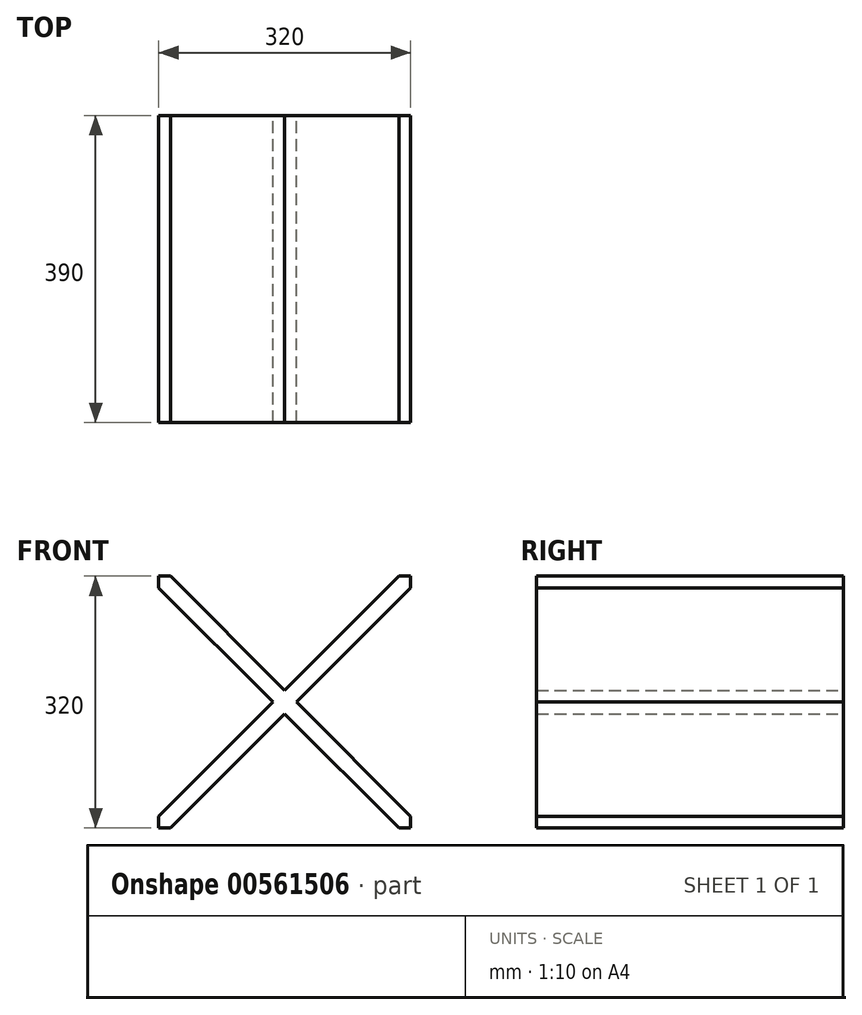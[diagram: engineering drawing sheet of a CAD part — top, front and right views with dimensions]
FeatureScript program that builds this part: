
annotation { "Feature Type Name" : "Feature", "Feature Type Description" : "" }
export const myFeature = defineFeature(function(context is Context, id is Id, definition is map)
    precondition{}
    {
        {
            var Q0;
            Q0=qCreatedBy(makeId("Front.planeOp"),FACE);
            var sketch = newSketch(context, id + "F0", { "sketchPlane" : qUnion([Q0])});
            skLineSegment(sketch, "E0.bottom", {"start": v(0, 0) * mm, "end": v(320, 0) * mm, "construction": true});
            skLineSegment(sketch, "E0.left", {"start": v(0, 0) * mm, "end": v(0, 320) * mm, "construction": true});
            skLineSegment(sketch, "E0.right", {"start": v(320, 0) * mm, "end": v(320, 320) * mm, "construction": true});
            skLineSegment(sketch, "E1", {"start": v(0, 320) * mm, "end": v(320, 0) * mm, "construction": true});
            skLineSegment(sketch, "E2", {"start": v(0, 0) * mm, "end": v(320, 320) * mm, "construction": true});
            skLineSegment(sketch, "E3", {"start": v(320, 320) * mm, "end": v(305, 320) * mm});
            skLineSegment(sketch, "E4", {"start": v(0, 0) * mm, "end": v(0, 15) * mm});
            skLineSegment(sketch, "E5", {"start": v(0, 15) * mm, "end": v(145, 160) * mm});
            skLineSegment(sketch, "E6.trimOffspring", {"start": v(305, 320) * mm, "end": v(320, 320) * mm, "construction": true});
            skLineSegment(sketch, "E7", {"start": v(0, 320) * mm, "end": v(320, 320) * mm, "construction": true});
            skLineSegment(sketch, "E8", {"start": v(0, 0) * mm, "end": v(15, 0) * mm});
            skLineSegment(sketch, "E9", {"start": v(15, 0) * mm, "end": v(160, 145) * mm});
            skLineSegment(sketch, "E10", {"start": v(320, 305) * mm, "end": v(320, 320) * mm});
            skLineSegment(sketch, "E11", {"start": v(0, 320) * mm, "end": v(15, 320) * mm});
            skLineSegment(sketch, "E12", {"start": v(15, 320) * mm, "end": v(320, 15) * mm});
            skLineSegment(sketch, "E13", {"start": v(320, 15) * mm, "end": v(320, 0) * mm});
            skLineSegment(sketch, "E14", {"start": v(320, 0) * mm, "end": v(305, 0) * mm});
            skLineSegment(sketch, "E15", {"start": v(305, 0) * mm, "end": v(160, 145) * mm});
            skLineSegment(sketch, "E16", {"start": v(0, 305) * mm, "end": v(0, 320) * mm});
            skLineSegment(sketch, "E17.trimOffspring", {"start": v(145, 160) * mm, "end": v(0, 305) * mm});
            skLineSegment(sketch, "E18.trimOffspring", {"start": v(175, 160) * mm, "end": v(320, 305) * mm});
            skLineSegment(sketch, "E19.trimOffspring", {"start": v(160, 175) * mm, "end": v(305, 320) * mm});
            skSolve(sketch);
        }
        {
            var Q0;
            Q0 = qSketchRegion(id + "F0", true);
            extrude(context, id + "F1", {"entities" : qUnion([Q0]), "depth" : 390 * mm, "offsetDistance" : 25 * mm, "symmetric" : true});
        }
    });
